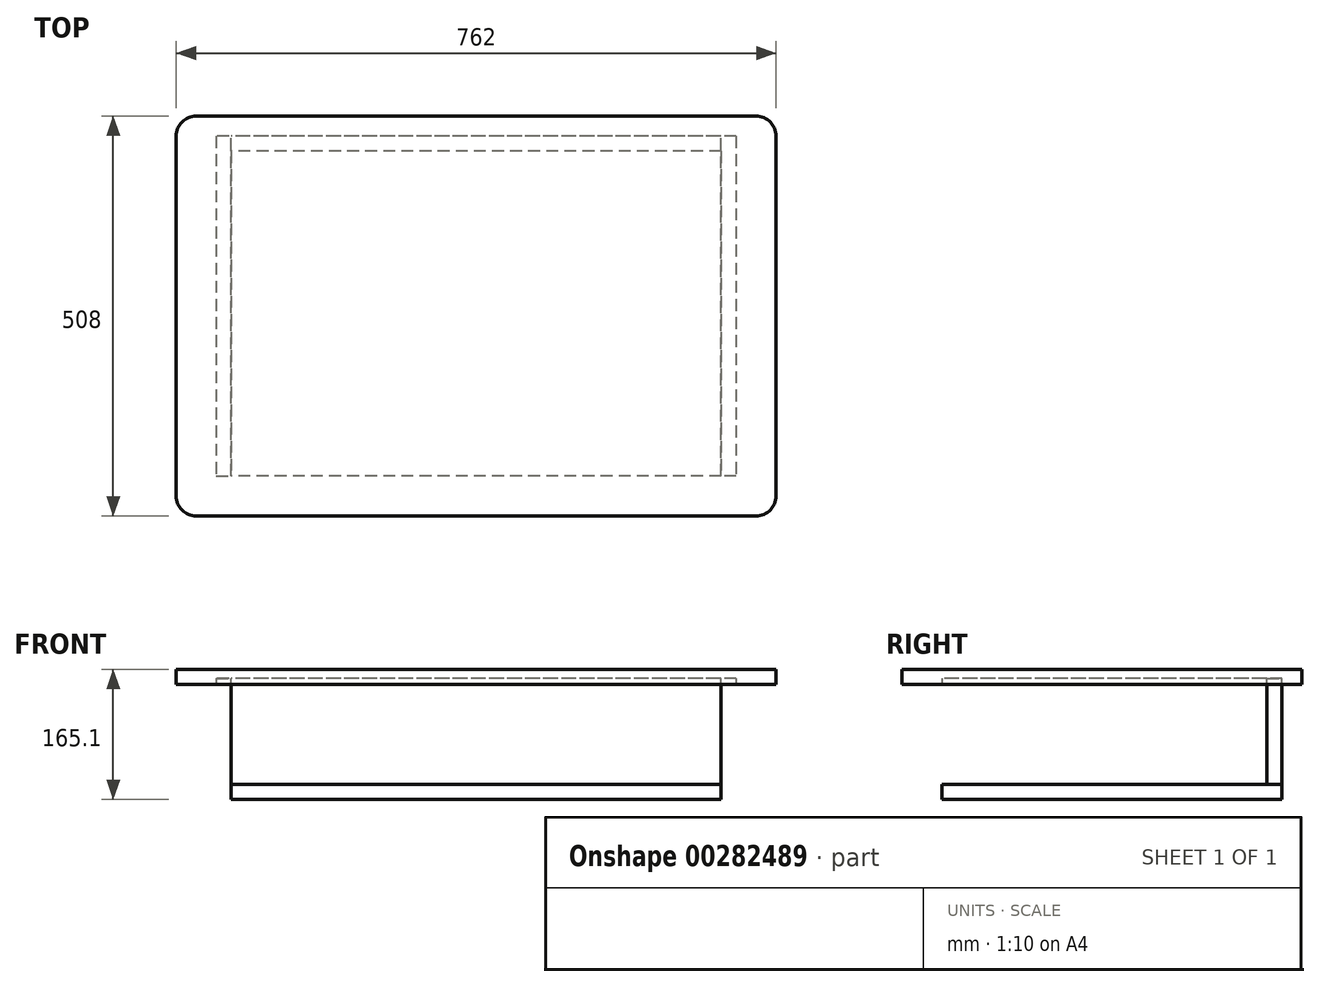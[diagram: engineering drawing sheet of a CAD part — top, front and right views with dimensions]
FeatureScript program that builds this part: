
annotation { "Feature Type Name" : "Feature", "Feature Type Description" : "" }
export const myFeature = defineFeature(function(context is Context, id is Id, definition is map)
    precondition{}
    {
        {
            var Q0;
            Q0=qCreatedBy(makeId("Top.planeOp"),FACE);
            var sketch = newSketch(context, id + "F0", { "sketchPlane" : qUnion([Q0])});
            skLineSegment(sketch, "E0.bottom", {"start": v(-355.6, 254) * mm, "end": v(355.6, 254) * mm});
            skLineSegment(sketch, "E0.top", {"start": v(-355.6, -254) * mm, "end": v(355.6, -254) * mm});
            skLineSegment(sketch, "E0.left", {"start": v(-381, 228.6) * mm, "end": v(-381, -228.6) * mm});
            skLineSegment(sketch, "E0.right", {"start": v(381, 228.6) * mm, "end": v(381, -228.6) * mm});
            skPoint(sketch, "E0.middle", {"position": v(0, 0) * mm});
            skPoint(sketch, "E1.visualSharp", {"position": v(381, 254) * mm});
            skArc(sketch, "E1.filletArc", {"start": v(381, 228.6) * mm, "mid": v(373.56, 246.56) * mm, "end": v(355.6, 254) * mm});
            skPoint(sketch, "E2.visualSharp", {"position": v(381, -254) * mm});
            skArc(sketch, "E2.filletArc", {"start": v(355.6, -254) * mm, "mid": v(373.56, -246.56) * mm, "end": v(381, -228.6) * mm});
            skPoint(sketch, "E3.visualSharp", {"position": v(-381, -254) * mm});
            skArc(sketch, "E3.filletArc", {"start": v(-381, -228.6) * mm, "mid": v(-373.56, -246.56) * mm, "end": v(-355.6, -254) * mm});
            skPoint(sketch, "E4.visualSharp", {"position": v(-381, 254) * mm});
            skArc(sketch, "E4.filletArc", {"start": v(-355.6, 254) * mm, "mid": v(-373.56, 246.56) * mm, "end": v(-381, 228.6) * mm});
            skSolve(sketch);
        }
        {
            var Q0;
            Q0 = qSketchRegion(id + "F0", true);
            extrude(context, id + "F1", {"entities" : qUnion([Q0]), "depth" : 19.05 * mm});
        }
        {
            var Q0;
            Q0=makeQuery(id+"F1.opExtrude","CAP_FACE",FACE,{"disambiguationData":[OSD([sQuery(id+"F0.wireOp",EDGE,"E0.bottom"),sQuery(id+"F0.wireOp",EDGE,"E0.top"),sQuery(id+"F0.wireOp",EDGE,"E0.left"),sQuery(id+"F0.wireOp",EDGE,"E0.right"),sQuery(id+"F0.wireOp",EDGE,"E1.filletArc"),sQuery(id+"F0.wireOp",EDGE,"E2.filletArc"),sQuery(id+"F0.wireOp",EDGE,"E3.filletArc"),sQuery(id+"F0.wireOp",EDGE,"E4.filletArc")])],"isStart":true});
            var sketch = newSketch(context, id + "F2", { "sketchPlane" : qUnion([Q0])});
            skLineSegment(sketch, "E5.bottom", {"start": v(330.2, -228.6) * mm, "end": v(-330.2, -228.6) * mm});
            skLineSegment(sketch, "E5.top", {"start": v(330.2, -209.55) * mm, "end": v(-330.2, -209.55) * mm});
            skLineSegment(sketch, "E5.left", {"start": v(330.2, -228.6) * mm, "end": v(330.2, -209.55) * mm});
            skLineSegment(sketch, "E5.right", {"start": v(-330.2, -228.6) * mm, "end": v(-330.2, -209.55) * mm});
            skLineSegment(sketch, "E6.top", {"start": v(330.2, 203.2) * mm, "end": v(311.15, 203.2) * mm});
            skLineSegment(sketch, "E6.left", {"start": v(330.2, -209.55) * mm, "end": v(330.2, 203.2) * mm});
            skLineSegment(sketch, "E6.right", {"start": v(311.15, -209.55) * mm, "end": v(311.15, 203.2) * mm});
            skLineSegment(sketch, "E7.bottom", {"start": v(-330.2, -209.55) * mm, "end": v(-311.15, -209.55) * mm});
            skLineSegment(sketch, "E7.top", {"start": v(-330.2, 203.2) * mm, "end": v(-311.15, 203.2) * mm});
            skLineSegment(sketch, "E7.left", {"start": v(-330.2, -209.55) * mm, "end": v(-330.2, 203.2) * mm});
            skLineSegment(sketch, "E7.right", {"start": v(-311.15, -209.55) * mm, "end": v(-311.15, 203.2) * mm});
            skSolve(sketch);
        }
        {
            var Q0;
            Q0 = qSketchRegion(id + "F2", true);
            extrude(context, id + "F3", {"entities" : qUnion([Q0]), "operationType" : NewBodyOperationType.REMOVE, "oppositeDirection" : true, "depth" : 7.62 * mm});
        }
        {
            var Q0;
            Q0=makeQuery(id+"F3.boolean.opBoolean","COPY",FACE,{"derivedFrom":makeQuery(id+"F3.opExtrude","CAP_FACE",FACE,{"disambiguationData":[OSD([sQuery(id+"F2.wireOp",EDGE,"E5.bottom"),sQuery(id+"F2.wireOp",EDGE,"E5.top"),sQuery(id+"F2.wireOp",EDGE,"E5.left"),sQuery(id+"F2.wireOp",EDGE,"E5.right"),sQuery(id+"F2.wireOp",EDGE,"E6.top"),sQuery(id+"F2.wireOp",EDGE,"E6.left"),sQuery(id+"F2.wireOp",EDGE,"E6.right"),sQuery(id+"F2.wireOp",EDGE,"E7.top"),sQuery(id+"F2.wireOp",EDGE,"E7.left"),sQuery(id+"F2.wireOp",EDGE,"E7.right")])],"isStart":false})});
            var sketch = newSketch(context, id + "F4", { "sketchPlane" : qUnion([Q0])});
            skLineSegment(sketch, "E8.bottom", {"start": v(311.15, -209.55) * mm, "end": v(-311.15, -209.55) * mm});
            skLineSegment(sketch, "E8.top", {"start": v(311.15, -228.6) * mm, "end": v(-311.15, -228.6) * mm});
            skLineSegment(sketch, "E8.left", {"start": v(311.15, -209.55) * mm, "end": v(311.15, -228.6) * mm});
            skLineSegment(sketch, "E8.right", {"start": v(-311.15, -209.55) * mm, "end": v(-311.15, -228.6) * mm});
            skSolve(sketch);
        }
        {
            var Q0;
            Q0=makeQuery(id+"F4.imprint","IMPRINT",FACE,{"disambiguationData":[TD([[makeQuery(id+"F4.imprint","IMPRINT",EDGE,{"derivedFrom":sQuery(id+"F4.wireOp",EDGE,"E8.bottom")}),1.0]])]});
            extrude(context, id + "F5", {"entities" : qUnion([Q0]), "depth" : 134.62 * mm});
        }
        {
            var Q0;
            Q0=makeQuery(id+"F5.opExtrude","CAP_FACE",FACE,{"disambiguationData":[OSD([sQuery(id+"F4.wireOp",EDGE,"E8.bottom"),sQuery(id+"F4.wireOp",EDGE,"E8.top"),sQuery(id+"F4.wireOp",EDGE,"E8.left"),sQuery(id+"F4.wireOp",EDGE,"E8.right")])],"isStart":false});
            var sketch = newSketch(context, id + "F6", { "sketchPlane" : qUnion([Q0])});
            skLineSegment(sketch, "E9.bottom", {"start": v(311.15, -228.6) * mm, "end": v(-311.15, -228.6) * mm});
            skLineSegment(sketch, "E9.top", {"start": v(311.15, 203.2) * mm, "end": v(-311.15, 203.2) * mm});
            skLineSegment(sketch, "E9.left", {"start": v(311.15, -228.6) * mm, "end": v(311.15, 203.2) * mm});
            skLineSegment(sketch, "E9.right", {"start": v(-311.15, -228.6) * mm, "end": v(-311.15, 203.2) * mm});
            skSolve(sketch);
        }
        {
            var Q0;
            Q0 = qSketchRegion(id + "F6", true);
            extrude(context, id + "F7", {"entities" : qUnion([Q0]), "depth" : 19.05 * mm});
        }
    });
